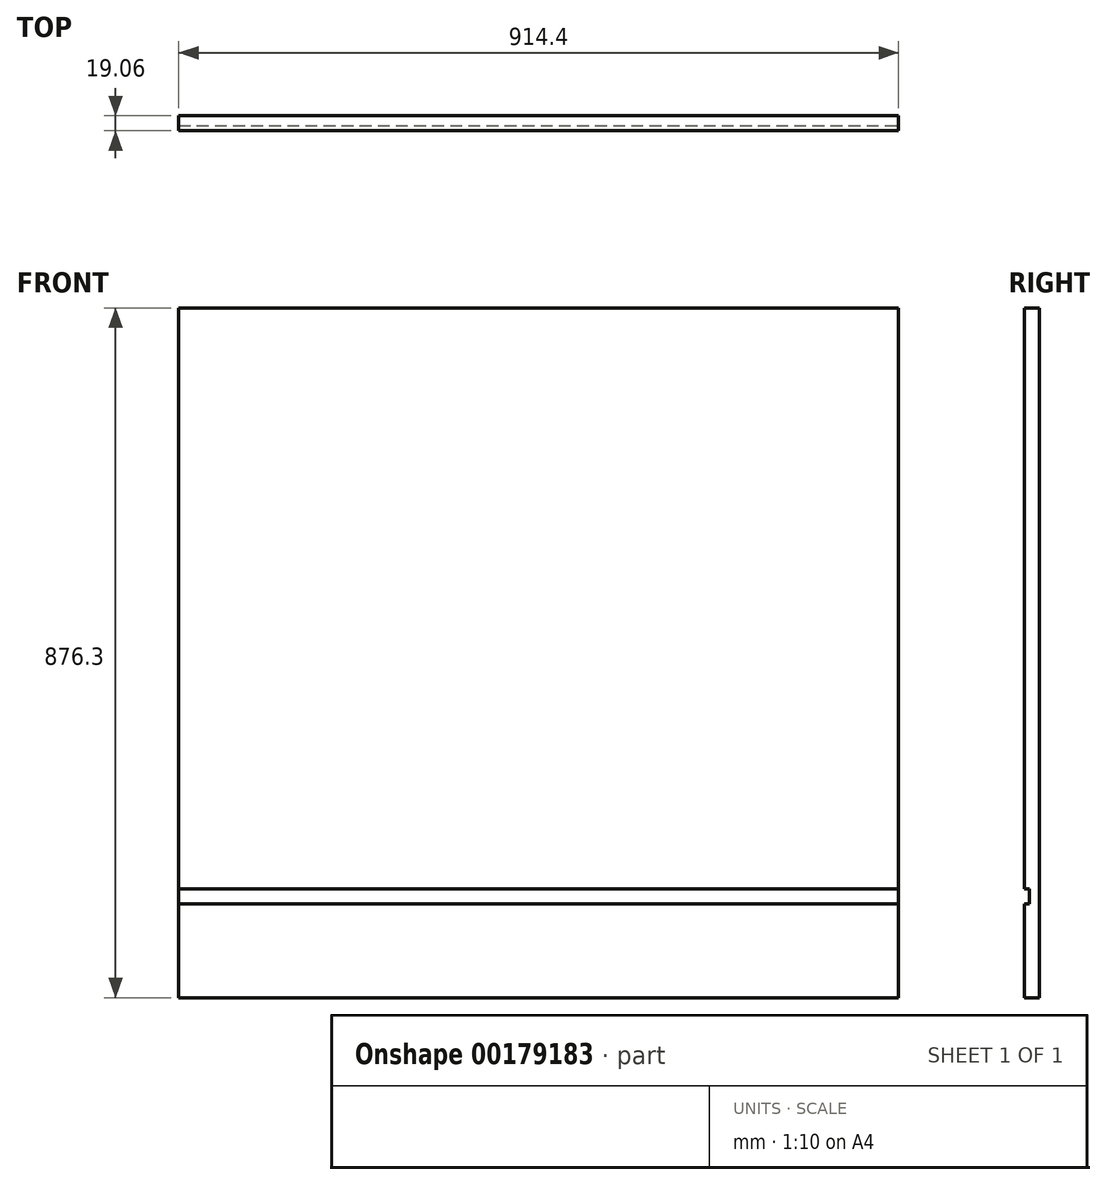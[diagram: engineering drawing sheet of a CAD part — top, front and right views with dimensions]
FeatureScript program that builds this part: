
annotation { "Feature Type Name" : "Feature", "Feature Type Description" : "" }
export const myFeature = defineFeature(function(context is Context, id is Id, definition is map)
    precondition{}
    {
        {
            var Q0;
            Q0=qCreatedBy(makeId("Front.planeOp"),FACE);
            var sketch = newSketch(context, id + "F0", { "sketchPlane" : qUnion([Q0])});
            skLineSegment(sketch, "E0.bottom", {"start": v(-247.9, 438.15) * mm, "end": v(666.5, 438.15) * mm});
            skLineSegment(sketch, "E0.top", {"start": v(-247.9, -438.15) * mm, "end": v(666.5, -438.15) * mm});
            skLineSegment(sketch, "E0.left", {"start": v(-247.9, 438.15) * mm, "end": v(-247.9, -438.15) * mm});
            skLineSegment(sketch, "E0.right", {"start": v(666.5, 438.15) * mm, "end": v(666.5, -438.15) * mm});
            skLineSegment(sketch, "E1", {"start": v(-247.9, 0) * mm, "end": v(666.5, 0) * mm});
            skSolve(sketch);
        }
        {
            var Q0;
            {var subQ0=sQuery(id+"F0.wireOp",EDGE,"E0.bottom");Q0=makeQuery(id+"F0.imprint","IMPRINT",FACE,{"disambiguationData":[TD([[makeQuery(id+"F0.imprint","IMPRINT",EDGE,{"derivedFrom":subQ0}),-1.0]])]});}
            var Q1;
            {var subQ0=sQuery(id+"F0.wireOp",EDGE,"E0.top");Q1=makeQuery(id+"F0.imprint","IMPRINT",FACE,{"disambiguationData":[TD([[makeQuery(id+"F0.imprint","IMPRINT",EDGE,{"derivedFrom":subQ0}),1.0]])]});}
            extrude(context, id + "F1", {"entities" : qUnion([Q0, Q1]), "depth" : 19.05 * mm, "symmetric" : true});
        }
        {
            var Q0;
            Q0=makeQuery(id+"F1.opExtrude","CAP_FACE",FACE,{"disambiguationData":[OSD([sQuery(id+"F0.wireOp",EDGE,"E0.bottom"),sQuery(id+"F0.wireOp",EDGE,"E0.top"),sQuery(id+"F0.wireOp",EDGE,"E0.left"),sQuery(id+"F0.wireOp",EDGE,"E0.right")])],"isStart":false});
            var sketch = newSketch(context, id + "F2", { "sketchPlane" : qUnion([Q0])});
            skLineSegment(sketch, "E2.bottom", {"start": v(666.5, 438.15) * mm, "end": v(647.45, 438.15) * mm});
            skLineSegment(sketch, "E2.top", {"start": v(666.5, -438.15) * mm, "end": v(647.45, -438.15) * mm});
            skLineSegment(sketch, "E2.left", {"start": v(666.5, 438.15) * mm, "end": v(666.5, -438.15) * mm});
            skLineSegment(sketch, "E2.right", {"start": v(647.45, 438.15) * mm, "end": v(647.45, -438.15) * mm});
            skSolve(sketch);
        }
        {
            var Q0;
            {var subQ0=sQuery(id+"F2.wireOp",EDGE,"E2.right");Q0=makeQuery(id+"F2.imprint","IMPRINT",FACE,{"disambiguationData":[TD([[makeQuery(id+"F2.imprint","IMPRINT",EDGE,{"derivedFrom":subQ0}),-1.0]])]});}
            var sketch = newSketch(context, id + "F3", { "sketchPlane" : qUnion([Q0])});
            skLineSegment(sketch, "E3.bottom", {"start": v(-247.9, -300.04) * mm, "end": v(666.5, -300.04) * mm});
            skLineSegment(sketch, "E3.top", {"start": v(-247.9, -319.09) * mm, "end": v(666.5, -319.09) * mm});
            skLineSegment(sketch, "E3.left", {"start": v(-247.9, -300.04) * mm, "end": v(-247.9, -319.09) * mm});
            skLineSegment(sketch, "E3.right", {"start": v(666.5, -300.04) * mm, "end": v(666.5, -319.09) * mm});
            skSolve(sketch);
        }
        {
            var Q0;
            Q0 = qSketchRegion(id + "F3", true);
            extrude(context, id + "F4", {"entities" : qUnion([Q0]), "operationType" : NewBodyOperationType.REMOVE, "oppositeDirection" : true, "depth" : 6.35 * mm});
        }
    });
